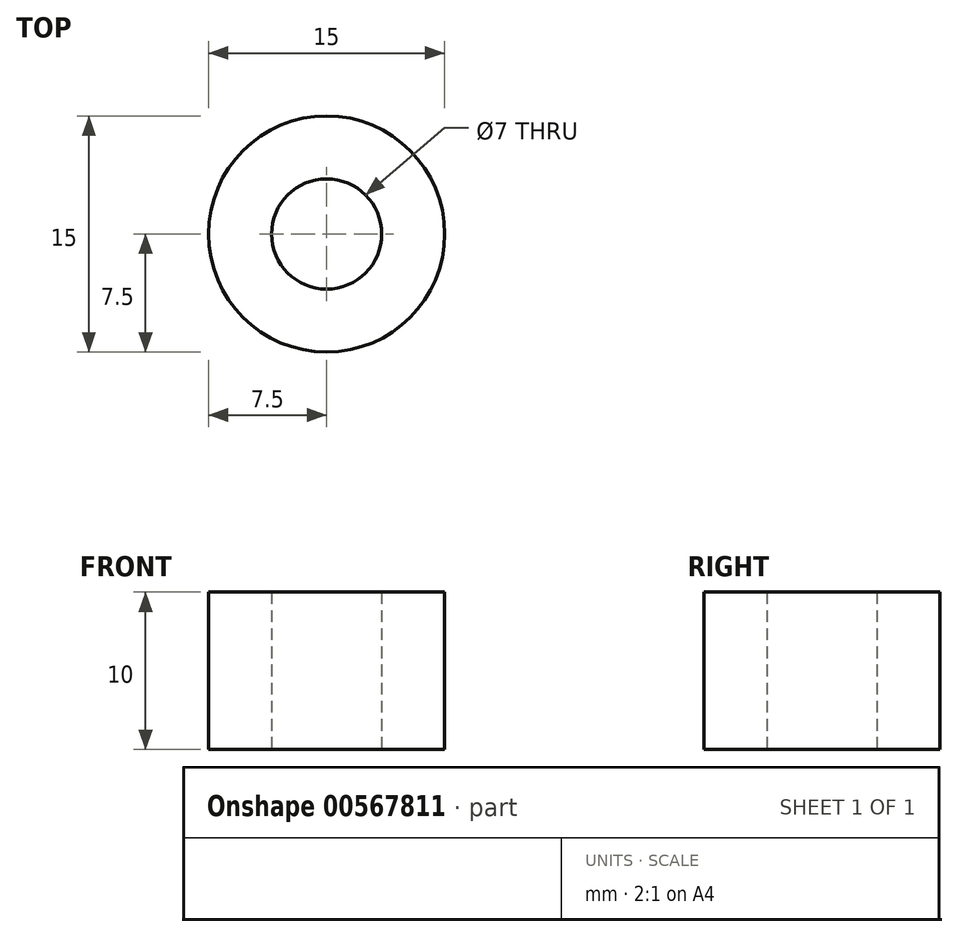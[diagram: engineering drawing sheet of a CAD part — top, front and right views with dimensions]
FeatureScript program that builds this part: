
annotation { "Feature Type Name" : "Feature", "Feature Type Description" : "" }
export const myFeature = defineFeature(function(context is Context, id is Id, definition is map)
    precondition{}
    {
        {
            var Q0;
            Q0=qCreatedBy(makeId("Top.planeOp"),FACE);
            var sketch = newSketch(context, id + "F0", { "sketchPlane" : qUnion([Q0])});
            skCircle(sketch, "E0", {"center": v(0, 0) * mm, "radius": 7.5 * mm});
            skCircle(sketch, "E1", {"center": v(0, 0) * mm, "radius": 3.5 * mm});
            skSolve(sketch);
        }
        {
            var Q0;
            Q0=makeQuery(id+"F0.imprint","IMPRINT",FACE,{"disambiguationData":[TD([[makeQuery(id+"F0.imprint","IMPRINT",EDGE,{"derivedFrom":sQuery(id+"F0.wireOp",EDGE,"E0")}),1.0]])]});
            var Q1;
            Q1=sQuery(id+"F0.wireOp",EDGE,"E1");
            extrude(context, id + "F1", {"entities" : qUnion([Q0]), "surfaceEntities" : qUnion([Q1]), "depth" : 10 * mm, "offsetDistance" : 25 * mm});
        }
    });
